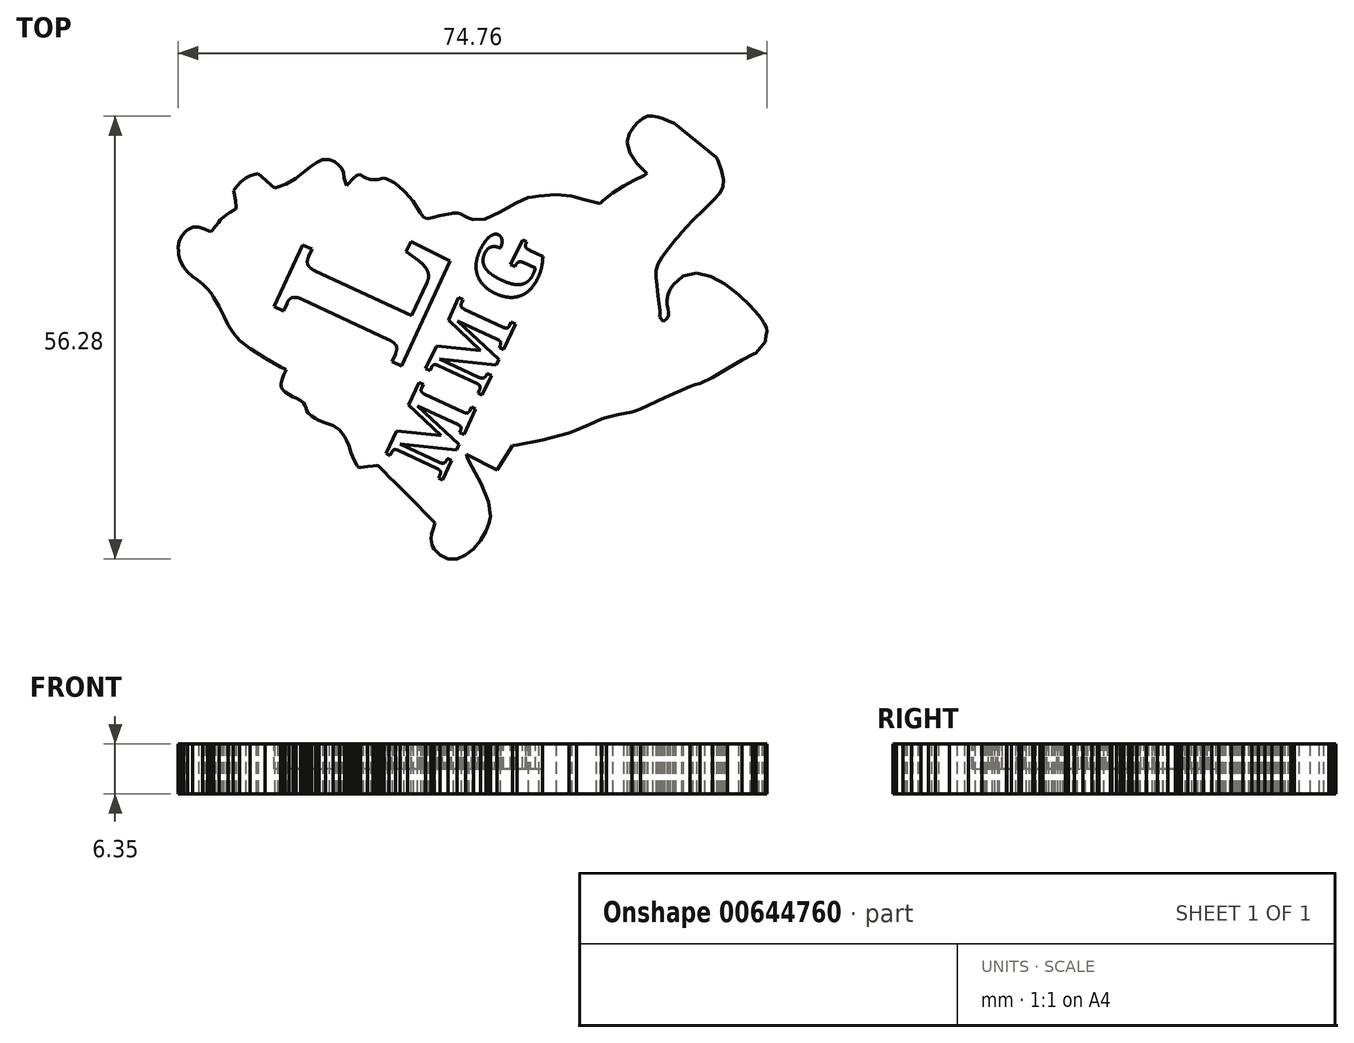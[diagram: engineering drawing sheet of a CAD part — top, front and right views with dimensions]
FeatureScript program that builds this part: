
annotation { "Feature Type Name" : "Feature", "Feature Type Description" : "" }
export const myFeature = defineFeature(function(context is Context, id is Id, definition is map)
    precondition{}
    {
        {
            var Q0;
            Q0=qCreatedBy(makeId("Top.planeOp"),FACE);
            var sketch = newSketch(context, id + "F0", { "sketchPlane" : qUnion([Q0])});
            skLineSegment(sketch, "E0", {"start": v(36, -1.99) * mm, "end": v(37.2, -0.53) * mm});
            skLineSegment(sketch, "E1", {"start": v(37.2, -0.53) * mm, "end": v(37.2, -0.33) * mm});
            skLineSegment(sketch, "E2", {"start": v(37.2, -0.33) * mm, "end": v(37.29, 0.26) * mm});
            skLineSegment(sketch, "E3", {"start": v(37.29, 0.26) * mm, "end": v(37.38, 0.75) * mm});
            skLineSegment(sketch, "E4", {"start": v(37.38, 0.75) * mm, "end": v(37.3, 1.24) * mm});
            skLineSegment(sketch, "E5", {"start": v(37.3, 1.24) * mm, "end": v(37, 1.85) * mm});
            skLineSegment(sketch, "E6", {"start": v(37, 1.85) * mm, "end": v(36.9, 2.04) * mm});
            skLineSegment(sketch, "E7", {"start": v(36.9, 2.04) * mm, "end": v(36.76, 2.25) * mm});
            skLineSegment(sketch, "E8", {"start": v(36.76, 2.25) * mm, "end": v(36.3, 2.84) * mm});
            skLineSegment(sketch, "E9", {"start": v(36.3, 2.84) * mm, "end": v(35.23, 4.06) * mm});
            skLineSegment(sketch, "E10", {"start": v(35.23, 4.06) * mm, "end": v(33.79, 5.46) * mm});
            skLineSegment(sketch, "E11", {"start": v(33.79, 5.46) * mm, "end": v(32.1, 6.77) * mm});
            skLineSegment(sketch, "E12", {"start": v(32.1, 6.77) * mm, "end": v(30.27, 7.76) * mm});
            skLineSegment(sketch, "E13", {"start": v(30.27, 7.76) * mm, "end": v(28.44, 8.18) * mm});
            skLineSegment(sketch, "E14", {"start": v(28.44, 8.18) * mm, "end": v(26.72, 7.78) * mm});
            skLineSegment(sketch, "E15", {"start": v(26.72, 7.78) * mm, "end": v(25.5, 6.74) * mm});
            skLineSegment(sketch, "E16", {"start": v(25.5, 6.74) * mm, "end": v(25.23, 6.3) * mm});
            skLineSegment(sketch, "E17", {"start": v(25.23, 6.3) * mm, "end": v(25.1, 6.12) * mm});
            skLineSegment(sketch, "E18", {"start": v(25.1, 6.12) * mm, "end": v(24.82, 5.48) * mm});
            skLineSegment(sketch, "E19", {"start": v(24.82, 5.48) * mm, "end": v(24.68, 4.78) * mm});
            skLineSegment(sketch, "E20", {"start": v(24.68, 4.78) * mm, "end": v(24.7, 4.17) * mm});
            skLineSegment(sketch, "E21", {"start": v(24.7, 4.17) * mm, "end": v(24.8, 3.65) * mm});
            skLineSegment(sketch, "E22", {"start": v(24.8, 3.65) * mm, "end": v(24.9, 3.2) * mm});
            skLineSegment(sketch, "E23", {"start": v(24.9, 3.2) * mm, "end": v(24.9, 2.8) * mm});
            skLineSegment(sketch, "E24", {"start": v(24.9, 2.8) * mm, "end": v(24.7, 2.42) * mm});
            skLineSegment(sketch, "E25", {"start": v(24.7, 2.42) * mm, "end": v(24.35, 2.14) * mm});
            skLineSegment(sketch, "E26", {"start": v(24.35, 2.14) * mm, "end": v(24.22, 2.07) * mm});
            skLineSegment(sketch, "E27", {"start": v(24.22, 2.07) * mm, "end": v(24.13, 2.18) * mm});
            skLineSegment(sketch, "E28", {"start": v(24.13, 2.18) * mm, "end": v(23.84, 2.5) * mm});
            skLineSegment(sketch, "E29", {"start": v(23.84, 2.5) * mm, "end": v(23.75, 2.6) * mm});
            skLineSegment(sketch, "E30", {"start": v(23.75, 2.6) * mm, "end": v(23.8, 2.8) * mm});
            skLineSegment(sketch, "E31", {"start": v(23.8, 2.8) * mm, "end": v(23.8, 3.28) * mm});
            skLineSegment(sketch, "E32", {"start": v(23.8, 3.28) * mm, "end": v(23.8, 3.44) * mm});
            skLineSegment(sketch, "E33", {"start": v(23.8, 3.44) * mm, "end": v(23.75, 3.9) * mm});
            skLineSegment(sketch, "E34", {"start": v(23.75, 3.9) * mm, "end": v(23.58, 5.26) * mm});
            skLineSegment(sketch, "E35", {"start": v(23.58, 5.26) * mm, "end": v(23.4, 6.62) * mm});
            skLineSegment(sketch, "E36", {"start": v(23.4, 6.62) * mm, "end": v(23.28, 7.67) * mm});
            skLineSegment(sketch, "E37", {"start": v(23.28, 7.67) * mm, "end": v(23.31, 8.52) * mm});
            skLineSegment(sketch, "E38", {"start": v(23.31, 8.52) * mm, "end": v(23.55, 9.33) * mm});
            skLineSegment(sketch, "E39", {"start": v(23.55, 9.33) * mm, "end": v(24.04, 10.22) * mm});
            skLineSegment(sketch, "E40", {"start": v(24.04, 10.22) * mm, "end": v(24.86, 11.32) * mm});
            skLineSegment(sketch, "E41", {"start": v(24.86, 11.32) * mm, "end": v(25.77, 12.41) * mm});
            skLineSegment(sketch, "E42", {"start": v(25.77, 12.41) * mm, "end": v(26.07, 12.77) * mm});
            skLineSegment(sketch, "E43", {"start": v(26.07, 12.77) * mm, "end": v(26.53, 13.3) * mm});
            skLineSegment(sketch, "E44", {"start": v(26.53, 13.3) * mm, "end": v(27.95, 14.84) * mm});
            skLineSegment(sketch, "E45", {"start": v(27.95, 14.84) * mm, "end": v(29.45, 16.34) * mm});
            skLineSegment(sketch, "E46", {"start": v(29.45, 16.34) * mm, "end": v(30.6, 17.44) * mm});
            skLineSegment(sketch, "E47", {"start": v(30.6, 17.44) * mm, "end": v(31.39, 18.31) * mm});
            skLineSegment(sketch, "E48", {"start": v(31.39, 18.31) * mm, "end": v(31.82, 19.12) * mm});
            skLineSegment(sketch, "E49", {"start": v(31.82, 19.12) * mm, "end": v(31.9, 20.03) * mm});
            skLineSegment(sketch, "E50", {"start": v(31.9, 20.03) * mm, "end": v(31.62, 21.22) * mm});
            skLineSegment(sketch, "E51", {"start": v(31.62, 21.22) * mm, "end": v(31.16, 22.44) * mm});
            skLineSegment(sketch, "E52", {"start": v(31.16, 22.44) * mm, "end": v(30.99, 22.84) * mm});
            skLineSegment(sketch, "E53", {"start": v(30.99, 22.84) * mm, "end": v(25.6, 27.24) * mm});
            skLineSegment(sketch, "E54", {"start": v(25.6, 27.24) * mm, "end": v(25.42, 27.3) * mm});
            skLineSegment(sketch, "E55", {"start": v(25.42, 27.3) * mm, "end": v(24.88, 27.5) * mm});
            skLineSegment(sketch, "E56", {"start": v(24.88, 27.5) * mm, "end": v(24.2, 27.79) * mm});
            skLineSegment(sketch, "E57", {"start": v(24.2, 27.79) * mm, "end": v(23.53, 28.02) * mm});
            skLineSegment(sketch, "E58", {"start": v(23.53, 28.02) * mm, "end": v(22.88, 28.14) * mm});
            skLineSegment(sketch, "E59", {"start": v(22.88, 28.14) * mm, "end": v(22.23, 28.1) * mm});
            skLineSegment(sketch, "E60", {"start": v(22.23, 28.1) * mm, "end": v(21.57, 27.81) * mm});
            skLineSegment(sketch, "E61", {"start": v(21.57, 27.81) * mm, "end": v(20.89, 27.24) * mm});
            skLineSegment(sketch, "E62", {"start": v(20.89, 27.24) * mm, "end": v(20.33, 26.55) * mm});
            skLineSegment(sketch, "E63", {"start": v(20.33, 26.55) * mm, "end": v(20.17, 26.3) * mm});
            skLineSegment(sketch, "E64", {"start": v(20.17, 26.3) * mm, "end": v(19.96, 25.98) * mm});
            skLineSegment(sketch, "E65", {"start": v(19.96, 25.98) * mm, "end": v(19.65, 24.8) * mm});
            skLineSegment(sketch, "E66", {"start": v(19.65, 24.8) * mm, "end": v(19.97, 23.43) * mm});
            skLineSegment(sketch, "E67", {"start": v(19.97, 23.43) * mm, "end": v(20.89, 22.11) * mm});
            skLineSegment(sketch, "E68", {"start": v(20.89, 22.11) * mm, "end": v(21.84, 21.12) * mm});
            skLineSegment(sketch, "E69", {"start": v(21.84, 21.12) * mm, "end": v(22.18, 20.8) * mm});
            skLineSegment(sketch, "E70", {"start": v(22.18, 20.8) * mm, "end": v(21.78, 20.59) * mm});
            skLineSegment(sketch, "E71", {"start": v(21.78, 20.59) * mm, "end": v(20.56, 19.98) * mm});
            skLineSegment(sketch, "E72", {"start": v(20.56, 19.98) * mm, "end": v(19.14, 19.26) * mm});
            skLineSegment(sketch, "E73", {"start": v(19.14, 19.26) * mm, "end": v(17.75, 18.35) * mm});
            skLineSegment(sketch, "E74", {"start": v(17.75, 18.35) * mm, "end": v(16.58, 17.37) * mm});
            skLineSegment(sketch, "E75", {"start": v(16.58, 17.37) * mm, "end": v(16.22, 17.02) * mm});
            skLineSegment(sketch, "E76", {"start": v(16.22, 17.02) * mm, "end": v(15.7, 17.11) * mm});
            skLineSegment(sketch, "E77", {"start": v(15.7, 17.11) * mm, "end": v(14.18, 17.51) * mm});
            skLineSegment(sketch, "E78", {"start": v(14.18, 17.51) * mm, "end": v(12.57, 17.95) * mm});
            skLineSegment(sketch, "E79", {"start": v(12.57, 17.95) * mm, "end": v(10.63, 18.13) * mm});
            skLineSegment(sketch, "E80", {"start": v(10.63, 18.13) * mm, "end": v(8.36, 17.97) * mm});
            skLineSegment(sketch, "E81", {"start": v(8.36, 17.97) * mm, "end": v(7.62, 17.86) * mm});
            skLineSegment(sketch, "E82", {"start": v(7.62, 17.86) * mm, "end": v(7.07, 17.77) * mm});
            skLineSegment(sketch, "E83", {"start": v(7.07, 17.77) * mm, "end": v(5.49, 17.1) * mm});
            skLineSegment(sketch, "E84", {"start": v(5.49, 17.1) * mm, "end": v(3.52, 15.94) * mm});
            skLineSegment(sketch, "E85", {"start": v(3.52, 15.94) * mm, "end": v(1.6, 15.06) * mm});
            skLineSegment(sketch, "E86", {"start": v(1.6, 15.06) * mm, "end": v(0.08, 14.95) * mm});
            skLineSegment(sketch, "E87", {"start": v(0.08, 14.95) * mm, "end": v(-0.35, 15.1) * mm});
            skLineSegment(sketch, "E88", {"start": v(-0.35, 15.1) * mm, "end": v(-0.53, 15.17) * mm});
            skLineSegment(sketch, "E89", {"start": v(-0.53, 15.17) * mm, "end": v(-1.03, 15.43) * mm});
            skLineSegment(sketch, "E90", {"start": v(-1.03, 15.43) * mm, "end": v(-1.44, 15.68) * mm});
            skLineSegment(sketch, "E91", {"start": v(-1.44, 15.68) * mm, "end": v(-1.9, 15.81) * mm});
            skLineSegment(sketch, "E92", {"start": v(-1.9, 15.81) * mm, "end": v(-2.48, 15.78) * mm});
            skLineSegment(sketch, "E93", {"start": v(-2.48, 15.78) * mm, "end": v(-2.67, 15.75) * mm});
            skLineSegment(sketch, "E94", {"start": v(-2.67, 15.75) * mm, "end": v(-3.03, 15.68) * mm});
            skLineSegment(sketch, "E95", {"start": v(-3.03, 15.68) * mm, "end": v(-4.11, 15.47) * mm});
            skLineSegment(sketch, "E96", {"start": v(-4.11, 15.47) * mm, "end": v(-5.07, 15.25) * mm});
            skLineSegment(sketch, "E97", {"start": v(-5.07, 15.25) * mm, "end": v(-5.67, 15.14) * mm});
            skLineSegment(sketch, "E98", {"start": v(-5.67, 15.14) * mm, "end": v(-6.05, 15.17) * mm});
            skLineSegment(sketch, "E99", {"start": v(-6.05, 15.17) * mm, "end": v(-6.32, 15.38) * mm});
            skLineSegment(sketch, "E100", {"start": v(-6.32, 15.38) * mm, "end": v(-6.61, 15.82) * mm});
            skLineSegment(sketch, "E101", {"start": v(-6.61, 15.82) * mm, "end": v(-7.05, 16.53) * mm});
            skLineSegment(sketch, "E102", {"start": v(-7.05, 16.53) * mm, "end": v(-7.56, 17.3) * mm});
            skLineSegment(sketch, "E103", {"start": v(-7.56, 17.3) * mm, "end": v(-7.75, 17.54) * mm});
            skLineSegment(sketch, "E104", {"start": v(-7.75, 17.54) * mm, "end": v(-7.87, 17.7) * mm});
            skLineSegment(sketch, "E105", {"start": v(-7.87, 17.7) * mm, "end": v(-8.74, 18.65) * mm});
            skLineSegment(sketch, "E106", {"start": v(-8.74, 18.65) * mm, "end": v(-9.8, 19.52) * mm});
            skLineSegment(sketch, "E107", {"start": v(-9.8, 19.52) * mm, "end": v(-10, 19.65) * mm});
            skLineSegment(sketch, "E108", {"start": v(-10, 19.65) * mm, "end": v(-10.2, 19.78) * mm});
            skLineSegment(sketch, "E109", {"start": v(-10.2, 19.78) * mm, "end": v(-10.84, 20.13) * mm});
            skLineSegment(sketch, "E110", {"start": v(-10.84, 20.13) * mm, "end": v(-11.25, 20.24) * mm});
            skLineSegment(sketch, "E111", {"start": v(-11.25, 20.24) * mm, "end": v(-11.57, 20.16) * mm});
            skLineSegment(sketch, "E112", {"start": v(-11.57, 20.16) * mm, "end": v(-11.98, 20.06) * mm});
            skLineSegment(sketch, "E113", {"start": v(-11.98, 20.06) * mm, "end": v(-12.12, 20.05) * mm});
            skLineSegment(sketch, "E114", {"start": v(-12.12, 20.05) * mm, "end": v(-12.33, 20.04) * mm});
            skLineSegment(sketch, "E115", {"start": v(-12.33, 20.04) * mm, "end": v(-12.96, 20.07) * mm});
            skLineSegment(sketch, "E116", {"start": v(-12.96, 20.07) * mm, "end": v(-13.51, 20.24) * mm});
            skLineSegment(sketch, "E117", {"start": v(-13.51, 20.24) * mm, "end": v(-13.88, 20.47) * mm});
            skLineSegment(sketch, "E118", {"start": v(-13.88, 20.47) * mm, "end": v(-14.15, 20.66) * mm});
            skLineSegment(sketch, "E119", {"start": v(-14.15, 20.66) * mm, "end": v(-14.41, 20.72) * mm});
            skLineSegment(sketch, "E120", {"start": v(-14.41, 20.72) * mm, "end": v(-14.74, 20.58) * mm});
            skLineSegment(sketch, "E121", {"start": v(-14.74, 20.58) * mm, "end": v(-15.24, 20.13) * mm});
            skLineSegment(sketch, "E122", {"start": v(-15.24, 20.13) * mm, "end": v(-15.8, 19.5) * mm});
            skLineSegment(sketch, "E123", {"start": v(-15.8, 19.5) * mm, "end": v(-15.99, 19.29) * mm});
            skLineSegment(sketch, "E124", {"start": v(-15.99, 19.29) * mm, "end": v(-16.1, 19.5) * mm});
            skLineSegment(sketch, "E125", {"start": v(-16.1, 19.5) * mm, "end": v(-16.3, 20.22) * mm});
            skLineSegment(sketch, "E126", {"start": v(-16.3, 20.22) * mm, "end": v(-16.4, 20.93) * mm});
            skLineSegment(sketch, "E127", {"start": v(-16.4, 20.93) * mm, "end": v(-16.64, 21.53) * mm});
            skLineSegment(sketch, "E128", {"start": v(-16.64, 21.53) * mm, "end": v(-17.15, 22.05) * mm});
            skLineSegment(sketch, "E129", {"start": v(-17.15, 22.05) * mm, "end": v(-17.34, 22.18) * mm});
            skLineSegment(sketch, "E130", {"start": v(-17.34, 22.18) * mm, "end": v(-17.55, 22.32) * mm});
            skLineSegment(sketch, "E131", {"start": v(-17.55, 22.32) * mm, "end": v(-18.25, 22.6) * mm});
            skLineSegment(sketch, "E132", {"start": v(-18.25, 22.6) * mm, "end": v(-19.07, 22.57) * mm});
            skLineSegment(sketch, "E133", {"start": v(-19.07, 22.57) * mm, "end": v(-19.85, 22.22) * mm});
            skLineSegment(sketch, "E134", {"start": v(-19.85, 22.22) * mm, "end": v(-20.64, 21.63) * mm});
            skLineSegment(sketch, "E135", {"start": v(-20.64, 21.63) * mm, "end": v(-21.5, 20.92) * mm});
            skLineSegment(sketch, "E136", {"start": v(-21.5, 20.92) * mm, "end": v(-22.5, 20.17) * mm});
            skLineSegment(sketch, "E137", {"start": v(-22.5, 20.17) * mm, "end": v(-23.7, 19.5) * mm});
            skLineSegment(sketch, "E138", {"start": v(-23.7, 19.5) * mm, "end": v(-24.78, 19.1) * mm});
            skLineSegment(sketch, "E139", {"start": v(-24.78, 19.1) * mm, "end": v(-25.15, 19) * mm});
            skLineSegment(sketch, "E140", {"start": v(-25.15, 19) * mm, "end": v(-27.25, 20.81) * mm});
            skLineSegment(sketch, "E141", {"start": v(-27.25, 20.81) * mm, "end": v(-27.48, 20.75) * mm});
            skLineSegment(sketch, "E142", {"start": v(-27.48, 20.75) * mm, "end": v(-28.18, 20.56) * mm});
            skLineSegment(sketch, "E143", {"start": v(-28.18, 20.56) * mm, "end": v(-28.85, 20.24) * mm});
            skLineSegment(sketch, "E144", {"start": v(-28.85, 20.24) * mm, "end": v(-29.5, 19.67) * mm});
            skLineSegment(sketch, "E145", {"start": v(-29.5, 19.67) * mm, "end": v(-30.17, 18.9) * mm});
            skLineSegment(sketch, "E146", {"start": v(-30.17, 18.9) * mm, "end": v(-30.38, 18.64) * mm});
            skLineSegment(sketch, "E147", {"start": v(-30.38, 18.64) * mm, "end": v(-30.32, 18.41) * mm});
            skLineSegment(sketch, "E148", {"start": v(-30.32, 18.41) * mm, "end": v(-30.1, 17.38) * mm});
            skLineSegment(sketch, "E149", {"start": v(-30.1, 17.38) * mm, "end": v(-30.06, 16.48) * mm});
            skLineSegment(sketch, "E150", {"start": v(-30.06, 16.48) * mm, "end": v(-30.09, 16.33) * mm});
            skLineSegment(sketch, "E151", {"start": v(-30.09, 16.33) * mm, "end": v(-30.27, 16.21) * mm});
            skLineSegment(sketch, "E152", {"start": v(-30.27, 16.21) * mm, "end": v(-30.83, 15.86) * mm});
            skLineSegment(sketch, "E153", {"start": v(-30.83, 15.86) * mm, "end": v(-31.33, 15.55) * mm});
            skLineSegment(sketch, "E154", {"start": v(-31.33, 15.55) * mm, "end": v(-31.64, 15.32) * mm});
            skLineSegment(sketch, "E155", {"start": v(-31.64, 15.32) * mm, "end": v(-31.85, 15.13) * mm});
            skLineSegment(sketch, "E156", {"start": v(-31.85, 15.13) * mm, "end": v(-32.04, 14.9) * mm});
            skLineSegment(sketch, "E157", {"start": v(-32.04, 14.9) * mm, "end": v(-32.28, 14.59) * mm});
            skLineSegment(sketch, "E158", {"start": v(-32.28, 14.59) * mm, "end": v(-32.66, 14.12) * mm});
            skLineSegment(sketch, "E159", {"start": v(-32.66, 14.12) * mm, "end": v(-33.09, 13.61) * mm});
            skLineSegment(sketch, "E160", {"start": v(-33.09, 13.61) * mm, "end": v(-33.23, 13.44) * mm});
            skLineSegment(sketch, "E161", {"start": v(-33.23, 13.44) * mm, "end": v(-33.45, 13.52) * mm});
            skLineSegment(sketch, "E162", {"start": v(-33.45, 13.52) * mm, "end": v(-34.07, 13.78) * mm});
            skLineSegment(sketch, "E163", {"start": v(-34.07, 13.78) * mm, "end": v(-34.79, 14.03) * mm});
            skLineSegment(sketch, "E164", {"start": v(-34.79, 14.03) * mm, "end": v(-35.5, 14.03) * mm});
            skLineSegment(sketch, "E165", {"start": v(-35.5, 14.03) * mm, "end": v(-36.13, 13.73) * mm});
            skLineSegment(sketch, "E166", {"start": v(-36.13, 13.73) * mm, "end": v(-36.3, 13.58) * mm});
            skLineSegment(sketch, "E167", {"start": v(-36.3, 13.58) * mm, "end": v(-36.49, 13.44) * mm});
            skLineSegment(sketch, "E168", {"start": v(-36.49, 13.44) * mm, "end": v(-36.94, 12.91) * mm});
            skLineSegment(sketch, "E169", {"start": v(-36.94, 12.91) * mm, "end": v(-37.27, 12.19) * mm});
            skLineSegment(sketch, "E170", {"start": v(-37.27, 12.19) * mm, "end": v(-37.38, 11.46) * mm});
            skLineSegment(sketch, "E171", {"start": v(-37.38, 11.46) * mm, "end": v(-37.37, 10.94) * mm});
            skLineSegment(sketch, "E172", {"start": v(-37.37, 10.94) * mm, "end": v(-37.35, 10.77) * mm});
            skLineSegment(sketch, "E173", {"start": v(-37.35, 10.77) * mm, "end": v(-37.32, 10.52) * mm});
            skLineSegment(sketch, "E174", {"start": v(-37.32, 10.52) * mm, "end": v(-37.13, 9.76) * mm});
            skLineSegment(sketch, "E175", {"start": v(-37.13, 9.76) * mm, "end": v(-36.73, 8.96) * mm});
            skLineSegment(sketch, "E176", {"start": v(-36.73, 8.96) * mm, "end": v(-36.21, 8.31) * mm});
            skLineSegment(sketch, "E177", {"start": v(-36.21, 8.31) * mm, "end": v(-35.6, 7.77) * mm});
            skLineSegment(sketch, "E178", {"start": v(-35.6, 7.77) * mm, "end": v(-34.94, 7.27) * mm});
            skLineSegment(sketch, "E179", {"start": v(-34.94, 7.27) * mm, "end": v(-34.28, 6.76) * mm});
            skLineSegment(sketch, "E180", {"start": v(-34.28, 6.76) * mm, "end": v(-33.65, 6.18) * mm});
            skLineSegment(sketch, "E181", {"start": v(-33.65, 6.18) * mm, "end": v(-33.23, 5.67) * mm});
            skLineSegment(sketch, "E182", {"start": v(-33.23, 5.67) * mm, "end": v(-33.1, 5.48) * mm});
            skLineSegment(sketch, "E183", {"start": v(-33.1, 5.48) * mm, "end": v(-32.87, 5.1) * mm});
            skLineSegment(sketch, "E184", {"start": v(-32.87, 5.1) * mm, "end": v(-32.22, 3.93) * mm});
            skLineSegment(sketch, "E185", {"start": v(-32.22, 3.93) * mm, "end": v(-31.6, 2.66) * mm});
            skLineSegment(sketch, "E186", {"start": v(-31.6, 2.66) * mm, "end": v(-31.06, 1.58) * mm});
            skLineSegment(sketch, "E187", {"start": v(-31.06, 1.58) * mm, "end": v(-30.44, 0.6) * mm});
            skLineSegment(sketch, "E188", {"start": v(-30.44, 0.6) * mm, "end": v(-29.57, -0.36) * mm});
            skLineSegment(sketch, "E189", {"start": v(-29.57, -0.36) * mm, "end": v(-28.27, -1.4) * mm});
            skLineSegment(sketch, "E190", {"start": v(-28.27, -1.4) * mm, "end": v(-26.37, -2.62) * mm});
            skLineSegment(sketch, "E191", {"start": v(-26.37, -2.62) * mm, "end": v(-24.37, -3.74) * mm});
            skLineSegment(sketch, "E192", {"start": v(-24.37, -3.74) * mm, "end": v(-23.7, -4.1) * mm});
            skLineSegment(sketch, "E193", {"start": v(-23.7, -4.1) * mm, "end": v(-23.77, -4.27) * mm});
            skLineSegment(sketch, "E194", {"start": v(-23.77, -4.27) * mm, "end": v(-23.99, -4.78) * mm});
            skLineSegment(sketch, "E195", {"start": v(-23.99, -4.78) * mm, "end": v(-24.2, -5.35) * mm});
            skLineSegment(sketch, "E196", {"start": v(-24.2, -5.35) * mm, "end": v(-24.32, -5.82) * mm});
            skLineSegment(sketch, "E197", {"start": v(-24.32, -5.82) * mm, "end": v(-24.32, -6.23) * mm});
            skLineSegment(sketch, "E198", {"start": v(-24.32, -6.23) * mm, "end": v(-24.16, -6.58) * mm});
            skLineSegment(sketch, "E199", {"start": v(-24.16, -6.58) * mm, "end": v(-23.84, -6.92) * mm});
            skLineSegment(sketch, "E200", {"start": v(-23.84, -6.92) * mm, "end": v(-23.33, -7.26) * mm});
            skLineSegment(sketch, "E201", {"start": v(-23.33, -7.26) * mm, "end": v(-22.78, -7.54) * mm});
            skLineSegment(sketch, "E202", {"start": v(-22.78, -7.54) * mm, "end": v(-22.6, -7.62) * mm});
            skLineSegment(sketch, "E203", {"start": v(-22.6, -7.62) * mm, "end": v(-22.41, -7.7) * mm});
            skLineSegment(sketch, "E204", {"start": v(-22.41, -7.7) * mm, "end": v(-21.87, -8) * mm});
            skLineSegment(sketch, "E205", {"start": v(-21.87, -8) * mm, "end": v(-21.46, -8.35) * mm});
            skLineSegment(sketch, "E206", {"start": v(-21.46, -8.35) * mm, "end": v(-21.25, -8.66) * mm});
            skLineSegment(sketch, "E207", {"start": v(-21.25, -8.66) * mm, "end": v(-21.16, -8.97) * mm});
            skLineSegment(sketch, "E208", {"start": v(-21.16, -8.97) * mm, "end": v(-21.06, -9.27) * mm});
            skLineSegment(sketch, "E209", {"start": v(-21.06, -9.27) * mm, "end": v(-20.87, -9.6) * mm});
            skLineSegment(sketch, "E210", {"start": v(-20.87, -9.6) * mm, "end": v(-20.48, -9.98) * mm});
            skLineSegment(sketch, "E211", {"start": v(-20.48, -9.98) * mm, "end": v(-19.96, -10.3) * mm});
            skLineSegment(sketch, "E212", {"start": v(-19.96, -10.3) * mm, "end": v(-19.78, -10.4) * mm});
            skLineSegment(sketch, "E213", {"start": v(-19.78, -10.4) * mm, "end": v(-19.52, -10.54) * mm});
            skLineSegment(sketch, "E214", {"start": v(-19.52, -10.54) * mm, "end": v(-18.68, -10.86) * mm});
            skLineSegment(sketch, "E215", {"start": v(-18.68, -10.86) * mm, "end": v(-17.73, -11.21) * mm});
            skLineSegment(sketch, "E216", {"start": v(-17.73, -11.21) * mm, "end": v(-16.88, -11.77) * mm});
            skLineSegment(sketch, "E217", {"start": v(-16.88, -11.77) * mm, "end": v(-16.26, -12.56) * mm});
            skLineSegment(sketch, "E218", {"start": v(-16.26, -12.56) * mm, "end": v(-16.1, -12.86) * mm});
            skLineSegment(sketch, "E219", {"start": v(-16.1, -12.86) * mm, "end": v(-15.99, -13.08) * mm});
            skLineSegment(sketch, "E220", {"start": v(-15.99, -13.08) * mm, "end": v(-15.7, -13.8) * mm});
            skLineSegment(sketch, "E221", {"start": v(-15.7, -13.8) * mm, "end": v(-15.42, -14.67) * mm});
            skLineSegment(sketch, "E222", {"start": v(-15.42, -14.67) * mm, "end": v(-15.07, -15.54) * mm});
            skLineSegment(sketch, "E223", {"start": v(-15.07, -15.54) * mm, "end": v(-14.65, -16.28) * mm});
            skLineSegment(sketch, "E224", {"start": v(-14.65, -16.28) * mm, "end": v(-14.49, -16.51) * mm});
            skLineSegment(sketch, "E225", {"start": v(-14.49, -16.51) * mm, "end": v(-14.2, -16.5) * mm});
            skLineSegment(sketch, "E226", {"start": v(-14.2, -16.5) * mm, "end": v(-13.36, -16.42) * mm});
            skLineSegment(sketch, "E227", {"start": v(-13.36, -16.42) * mm, "end": v(-12.65, -16.32) * mm});
            skLineSegment(sketch, "E228", {"start": v(-12.65, -16.32) * mm, "end": v(-12.22, -16.28) * mm});
            skLineSegment(sketch, "E229", {"start": v(-12.22, -16.28) * mm, "end": v(-11.94, -16.34) * mm});
            skLineSegment(sketch, "E230", {"start": v(-11.94, -16.34) * mm, "end": v(-11.66, -16.56) * mm});
            skLineSegment(sketch, "E231", {"start": v(-11.66, -16.56) * mm, "end": v(-11.26, -17) * mm});
            skLineSegment(sketch, "E232", {"start": v(-11.26, -17) * mm, "end": v(-10.6, -17.72) * mm});
            skLineSegment(sketch, "E233", {"start": v(-10.6, -17.72) * mm, "end": v(-9.8, -18.51) * mm});
            skLineSegment(sketch, "E234", {"start": v(-9.8, -18.51) * mm, "end": v(-9.52, -18.77) * mm});
            skLineSegment(sketch, "E235", {"start": v(-9.52, -18.77) * mm, "end": v(-9.2, -19.07) * mm});
            skLineSegment(sketch, "E236", {"start": v(-9.2, -19.07) * mm, "end": v(-8.25, -20) * mm});
            skLineSegment(sketch, "E237", {"start": v(-8.25, -20) * mm, "end": v(-7.1, -21.18) * mm});
            skLineSegment(sketch, "E238", {"start": v(-7.1, -21.18) * mm, "end": v(-5.98, -22.34) * mm});
            skLineSegment(sketch, "E239", {"start": v(-5.98, -22.34) * mm, "end": v(-5.07, -23.25) * mm});
            skLineSegment(sketch, "E240", {"start": v(-5.07, -23.25) * mm, "end": v(-4.76, -23.55) * mm});
            skLineSegment(sketch, "E241", {"start": v(-4.76, -23.55) * mm, "end": v(-4.8, -23.76) * mm});
            skLineSegment(sketch, "E242", {"start": v(-4.8, -23.76) * mm, "end": v(-5, -24.36) * mm});
            skLineSegment(sketch, "E243", {"start": v(-5, -24.36) * mm, "end": v(-5.2, -24.98) * mm});
            skLineSegment(sketch, "E244", {"start": v(-5.2, -24.98) * mm, "end": v(-5.26, -25.63) * mm});
            skLineSegment(sketch, "E245", {"start": v(-5.26, -25.63) * mm, "end": v(-5.16, -26.33) * mm});
            skLineSegment(sketch, "E246", {"start": v(-5.16, -26.33) * mm, "end": v(-5.1, -26.55) * mm});
            skLineSegment(sketch, "E247", {"start": v(-5.1, -26.55) * mm, "end": v(-4.92, -26.86) * mm});
            skLineSegment(sketch, "E248", {"start": v(-4.92, -26.86) * mm, "end": v(-4.15, -27.65) * mm});
            skLineSegment(sketch, "E249", {"start": v(-4.15, -27.65) * mm, "end": v(-3.1, -28.14) * mm});
            skLineSegment(sketch, "E250", {"start": v(-3.1, -28.14) * mm, "end": v(-1.99, -28.11) * mm});
            skLineSegment(sketch, "E251", {"start": v(-1.99, -28.11) * mm, "end": v(-0.9, -27.65) * mm});
            skLineSegment(sketch, "E252", {"start": v(-0.9, -27.65) * mm, "end": v(0.13, -26.85) * mm});
            skLineSegment(sketch, "E253", {"start": v(0.13, -26.85) * mm, "end": v(1.02, -25.8) * mm});
            skLineSegment(sketch, "E254", {"start": v(1.02, -25.8) * mm, "end": v(1.71, -24.57) * mm});
            skLineSegment(sketch, "E255", {"start": v(1.71, -24.57) * mm, "end": v(2.08, -23.6) * mm});
            skLineSegment(sketch, "E256", {"start": v(2.08, -23.6) * mm, "end": v(2.16, -23.26) * mm});
            skLineSegment(sketch, "E257", {"start": v(2.16, -23.26) * mm, "end": v(2.28, -22.72) * mm});
            skLineSegment(sketch, "E258", {"start": v(2.28, -22.72) * mm, "end": v(2.03, -20.93) * mm});
            skLineSegment(sketch, "E259", {"start": v(2.03, -20.93) * mm, "end": v(1.07, -18.56) * mm});
            skLineSegment(sketch, "E260", {"start": v(1.07, -18.56) * mm, "end": v(-0.07, -16.43) * mm});
            skLineSegment(sketch, "E261", {"start": v(-0.07, -16.43) * mm, "end": v(-0.68, -15.26) * mm});
            skLineSegment(sketch, "E262", {"start": v(-0.68, -15.26) * mm, "end": v(-0.76, -14.85) * mm});
            skLineSegment(sketch, "E263", {"start": v(-0.76, -14.85) * mm, "end": v(3.1, -16.84) * mm});
            skLineSegment(sketch, "E264", {"start": v(3.1, -16.84) * mm, "end": v(5.05, -13.71) * mm});
            skLineSegment(sketch, "E265", {"start": v(5.05, -13.71) * mm, "end": v(5.62, -13.66) * mm});
            skLineSegment(sketch, "E266", {"start": v(5.62, -13.66) * mm, "end": v(8.9, -13.05) * mm});
            skLineSegment(sketch, "E267", {"start": v(8.9, -13.05) * mm, "end": v(12.27, -12.12) * mm});
            skLineSegment(sketch, "E268", {"start": v(12.27, -12.12) * mm, "end": v(12.88, -11.9) * mm});
            skLineSegment(sketch, "E269", {"start": v(12.88, -11.9) * mm, "end": v(13.23, -11.79) * mm});
            skLineSegment(sketch, "E270", {"start": v(13.23, -11.79) * mm, "end": v(14.83, -11.08) * mm});
            skLineSegment(sketch, "E271", {"start": v(14.83, -11.08) * mm, "end": v(16.4, -10.37) * mm});
            skLineSegment(sketch, "E272", {"start": v(16.4, -10.37) * mm, "end": v(16.73, -10.24) * mm});
            skLineSegment(sketch, "E273", {"start": v(16.73, -10.24) * mm, "end": v(17.01, -10.14) * mm});
            skLineSegment(sketch, "E274", {"start": v(17.01, -10.14) * mm, "end": v(18.54, -9.81) * mm});
            skLineSegment(sketch, "E275", {"start": v(18.54, -9.81) * mm, "end": v(20.26, -9.44) * mm});
            skLineSegment(sketch, "E276", {"start": v(20.26, -9.44) * mm, "end": v(20.63, -9.31) * mm});
            skLineSegment(sketch, "E277", {"start": v(20.63, -9.31) * mm, "end": v(21.3, -9.08) * mm});
            skLineSegment(sketch, "E278", {"start": v(21.3, -9.08) * mm, "end": v(24.47, -7.65) * mm});
            skLineSegment(sketch, "E279", {"start": v(24.47, -7.65) * mm, "end": v(27.64, -6.23) * mm});
            skLineSegment(sketch, "E280", {"start": v(27.64, -6.23) * mm, "end": v(28.3, -6) * mm});
            skLineSegment(sketch, "E281", {"start": v(28.3, -6) * mm, "end": v(28.86, -5.82) * mm});
            skLineSegment(sketch, "E282", {"start": v(28.86, -5.82) * mm, "end": v(30.46, -5.08) * mm});
            skLineSegment(sketch, "E283", {"start": v(30.46, -5.08) * mm, "end": v(32.4, -3.97) * mm});
            skLineSegment(sketch, "E284", {"start": v(32.4, -3.97) * mm, "end": v(34.2, -2.87) * mm});
            skLineSegment(sketch, "E285", {"start": v(34.2, -2.87) * mm, "end": v(35.54, -2.17) * mm});
            skLineSegment(sketch, "E286", {"start": v(35.54, -2.17) * mm, "end": v(36, -1.99) * mm});
            skSolve(sketch);
        }
        {
            var Q0;
            Q0=makeQuery(id+"F0.imprint","IMPRINT",FACE,{"disambiguationData":[TD([[makeQuery(id+"F0.imprint","IMPRINT",EDGE,{"derivedFrom":sQuery(id+"F0.wireOp",EDGE,"E0")}),1.0]])]});
            extrude(context, id + "F1", {"entities" : qUnion([Q0]), "depth" : 6.35 * mm, "offsetDistance" : 25.4 * mm});
        }
        {
            var Q0;
            Q0=makeQuery(id+"F1.opExtrude","CAP_FACE",FACE,{"disambiguationData":[OSD([sQuery(id+"F0.wireOp",EDGE,"E0"),sQuery(id+"F0.wireOp",EDGE,"E1"),sQuery(id+"F0.wireOp",EDGE,"E2"),sQuery(id+"F0.wireOp",EDGE,"E3"),sQuery(id+"F0.wireOp",EDGE,"E4"),sQuery(id+"F0.wireOp",EDGE,"E5"),sQuery(id+"F0.wireOp",EDGE,"E6"),sQuery(id+"F0.wireOp",EDGE,"E7"),sQuery(id+"F0.wireOp",EDGE,"E8"),sQuery(id+"F0.wireOp",EDGE,"E9"),sQuery(id+"F0.wireOp",EDGE,"E10"),sQuery(id+"F0.wireOp",EDGE,"E11"),sQuery(id+"F0.wireOp",EDGE,"E12"),sQuery(id+"F0.wireOp",EDGE,"E13"),sQuery(id+"F0.wireOp",EDGE,"E14"),sQuery(id+"F0.wireOp",EDGE,"E15"),sQuery(id+"F0.wireOp",EDGE,"E16"),sQuery(id+"F0.wireOp",EDGE,"E17"),sQuery(id+"F0.wireOp",EDGE,"E18"),sQuery(id+"F0.wireOp",EDGE,"E19"),sQuery(id+"F0.wireOp",EDGE,"E20"),sQuery(id+"F0.wireOp",EDGE,"E21"),sQuery(id+"F0.wireOp",EDGE,"E22"),sQuery(id+"F0.wireOp",EDGE,"E23"),sQuery(id+"F0.wireOp",EDGE,"E24"),sQuery(id+"F0.wireOp",EDGE,"E25"),sQuery(id+"F0.wireOp",EDGE,"E26"),sQuery(id+"F0.wireOp",EDGE,"E27"),sQuery(id+"F0.wireOp",EDGE,"E28"),sQuery(id+"F0.wireOp",EDGE,"E29"),sQuery(id+"F0.wireOp",EDGE,"E30"),sQuery(id+"F0.wireOp",EDGE,"E31"),sQuery(id+"F0.wireOp",EDGE,"E32"),sQuery(id+"F0.wireOp",EDGE,"E33"),sQuery(id+"F0.wireOp",EDGE,"E34"),sQuery(id+"F0.wireOp",EDGE,"E35"),sQuery(id+"F0.wireOp",EDGE,"E36"),sQuery(id+"F0.wireOp",EDGE,"E37"),sQuery(id+"F0.wireOp",EDGE,"E38"),sQuery(id+"F0.wireOp",EDGE,"E39"),sQuery(id+"F0.wireOp",EDGE,"E40"),sQuery(id+"F0.wireOp",EDGE,"E41"),sQuery(id+"F0.wireOp",EDGE,"E42"),sQuery(id+"F0.wireOp",EDGE,"E43"),sQuery(id+"F0.wireOp",EDGE,"E44"),sQuery(id+"F0.wireOp",EDGE,"E45"),sQuery(id+"F0.wireOp",EDGE,"E46"),sQuery(id+"F0.wireOp",EDGE,"E47"),sQuery(id+"F0.wireOp",EDGE,"E48"),sQuery(id+"F0.wireOp",EDGE,"E49"),sQuery(id+"F0.wireOp",EDGE,"E50"),sQuery(id+"F0.wireOp",EDGE,"E51"),sQuery(id+"F0.wireOp",EDGE,"E52"),sQuery(id+"F0.wireOp",EDGE,"E53"),sQuery(id+"F0.wireOp",EDGE,"E54"),sQuery(id+"F0.wireOp",EDGE,"E55"),sQuery(id+"F0.wireOp",EDGE,"E56"),sQuery(id+"F0.wireOp",EDGE,"E57"),sQuery(id+"F0.wireOp",EDGE,"E58"),sQuery(id+"F0.wireOp",EDGE,"E59"),sQuery(id+"F0.wireOp",EDGE,"E60"),sQuery(id+"F0.wireOp",EDGE,"E61"),sQuery(id+"F0.wireOp",EDGE,"E62"),sQuery(id+"F0.wireOp",EDGE,"E63"),sQuery(id+"F0.wireOp",EDGE,"E64"),sQuery(id+"F0.wireOp",EDGE,"E65"),sQuery(id+"F0.wireOp",EDGE,"E66"),sQuery(id+"F0.wireOp",EDGE,"E67"),sQuery(id+"F0.wireOp",EDGE,"E68"),sQuery(id+"F0.wireOp",EDGE,"E69"),sQuery(id+"F0.wireOp",EDGE,"E70"),sQuery(id+"F0.wireOp",EDGE,"E71"),sQuery(id+"F0.wireOp",EDGE,"E72"),sQuery(id+"F0.wireOp",EDGE,"E73"),sQuery(id+"F0.wireOp",EDGE,"E74"),sQuery(id+"F0.wireOp",EDGE,"E75"),sQuery(id+"F0.wireOp",EDGE,"E76"),sQuery(id+"F0.wireOp",EDGE,"E77"),sQuery(id+"F0.wireOp",EDGE,"E78"),sQuery(id+"F0.wireOp",EDGE,"E79"),sQuery(id+"F0.wireOp",EDGE,"E80"),sQuery(id+"F0.wireOp",EDGE,"E81"),sQuery(id+"F0.wireOp",EDGE,"E82"),sQuery(id+"F0.wireOp",EDGE,"E83"),sQuery(id+"F0.wireOp",EDGE,"E84"),sQuery(id+"F0.wireOp",EDGE,"E85"),sQuery(id+"F0.wireOp",EDGE,"E86"),sQuery(id+"F0.wireOp",EDGE,"E87"),sQuery(id+"F0.wireOp",EDGE,"E88"),sQuery(id+"F0.wireOp",EDGE,"E89"),sQuery(id+"F0.wireOp",EDGE,"E90"),sQuery(id+"F0.wireOp",EDGE,"E91"),sQuery(id+"F0.wireOp",EDGE,"E92"),sQuery(id+"F0.wireOp",EDGE,"E93"),sQuery(id+"F0.wireOp",EDGE,"E94"),sQuery(id+"F0.wireOp",EDGE,"E95"),sQuery(id+"F0.wireOp",EDGE,"E96"),sQuery(id+"F0.wireOp",EDGE,"E97"),sQuery(id+"F0.wireOp",EDGE,"E98"),sQuery(id+"F0.wireOp",EDGE,"E99"),sQuery(id+"F0.wireOp",EDGE,"E100"),sQuery(id+"F0.wireOp",EDGE,"E101"),sQuery(id+"F0.wireOp",EDGE,"E102"),sQuery(id+"F0.wireOp",EDGE,"E103"),sQuery(id+"F0.wireOp",EDGE,"E104"),sQuery(id+"F0.wireOp",EDGE,"E105"),sQuery(id+"F0.wireOp",EDGE,"E106"),sQuery(id+"F0.wireOp",EDGE,"E107"),sQuery(id+"F0.wireOp",EDGE,"E108"),sQuery(id+"F0.wireOp",EDGE,"E109"),sQuery(id+"F0.wireOp",EDGE,"E110"),sQuery(id+"F0.wireOp",EDGE,"E111"),sQuery(id+"F0.wireOp",EDGE,"E112"),sQuery(id+"F0.wireOp",EDGE,"E113"),sQuery(id+"F0.wireOp",EDGE,"E114"),sQuery(id+"F0.wireOp",EDGE,"E115"),sQuery(id+"F0.wireOp",EDGE,"E116"),sQuery(id+"F0.wireOp",EDGE,"E117"),sQuery(id+"F0.wireOp",EDGE,"E118"),sQuery(id+"F0.wireOp",EDGE,"E119"),sQuery(id+"F0.wireOp",EDGE,"E120"),sQuery(id+"F0.wireOp",EDGE,"E121"),sQuery(id+"F0.wireOp",EDGE,"E122"),sQuery(id+"F0.wireOp",EDGE,"E123"),sQuery(id+"F0.wireOp",EDGE,"E124"),sQuery(id+"F0.wireOp",EDGE,"E125"),sQuery(id+"F0.wireOp",EDGE,"E126"),sQuery(id+"F0.wireOp",EDGE,"E127"),sQuery(id+"F0.wireOp",EDGE,"E128"),sQuery(id+"F0.wireOp",EDGE,"E129"),sQuery(id+"F0.wireOp",EDGE,"E130"),sQuery(id+"F0.wireOp",EDGE,"E131"),sQuery(id+"F0.wireOp",EDGE,"E132"),sQuery(id+"F0.wireOp",EDGE,"E133"),sQuery(id+"F0.wireOp",EDGE,"E134"),sQuery(id+"F0.wireOp",EDGE,"E135"),sQuery(id+"F0.wireOp",EDGE,"E136"),sQuery(id+"F0.wireOp",EDGE,"E137"),sQuery(id+"F0.wireOp",EDGE,"E138"),sQuery(id+"F0.wireOp",EDGE,"E139"),sQuery(id+"F0.wireOp",EDGE,"E140"),sQuery(id+"F0.wireOp",EDGE,"E141"),sQuery(id+"F0.wireOp",EDGE,"E142"),sQuery(id+"F0.wireOp",EDGE,"E143"),sQuery(id+"F0.wireOp",EDGE,"E144"),sQuery(id+"F0.wireOp",EDGE,"E145"),sQuery(id+"F0.wireOp",EDGE,"E146"),sQuery(id+"F0.wireOp",EDGE,"E147"),sQuery(id+"F0.wireOp",EDGE,"E148"),sQuery(id+"F0.wireOp",EDGE,"E149"),sQuery(id+"F0.wireOp",EDGE,"E150"),sQuery(id+"F0.wireOp",EDGE,"E151"),sQuery(id+"F0.wireOp",EDGE,"E152"),sQuery(id+"F0.wireOp",EDGE,"E153"),sQuery(id+"F0.wireOp",EDGE,"E154"),sQuery(id+"F0.wireOp",EDGE,"E155"),sQuery(id+"F0.wireOp",EDGE,"E156"),sQuery(id+"F0.wireOp",EDGE,"E157"),sQuery(id+"F0.wireOp",EDGE,"E158"),sQuery(id+"F0.wireOp",EDGE,"E159"),sQuery(id+"F0.wireOp",EDGE,"E160"),sQuery(id+"F0.wireOp",EDGE,"E161"),sQuery(id+"F0.wireOp",EDGE,"E162"),sQuery(id+"F0.wireOp",EDGE,"E163"),sQuery(id+"F0.wireOp",EDGE,"E164"),sQuery(id+"F0.wireOp",EDGE,"E165"),sQuery(id+"F0.wireOp",EDGE,"E166"),sQuery(id+"F0.wireOp",EDGE,"E167"),sQuery(id+"F0.wireOp",EDGE,"E168"),sQuery(id+"F0.wireOp",EDGE,"E169"),sQuery(id+"F0.wireOp",EDGE,"E170"),sQuery(id+"F0.wireOp",EDGE,"E171"),sQuery(id+"F0.wireOp",EDGE,"E172"),sQuery(id+"F0.wireOp",EDGE,"E173"),sQuery(id+"F0.wireOp",EDGE,"E174"),sQuery(id+"F0.wireOp",EDGE,"E175"),sQuery(id+"F0.wireOp",EDGE,"E176"),sQuery(id+"F0.wireOp",EDGE,"E177"),sQuery(id+"F0.wireOp",EDGE,"E178"),sQuery(id+"F0.wireOp",EDGE,"E179"),sQuery(id+"F0.wireOp",EDGE,"E180"),sQuery(id+"F0.wireOp",EDGE,"E181"),sQuery(id+"F0.wireOp",EDGE,"E182"),sQuery(id+"F0.wireOp",EDGE,"E183"),sQuery(id+"F0.wireOp",EDGE,"E184"),sQuery(id+"F0.wireOp",EDGE,"E185"),sQuery(id+"F0.wireOp",EDGE,"E186"),sQuery(id+"F0.wireOp",EDGE,"E187"),sQuery(id+"F0.wireOp",EDGE,"E188"),sQuery(id+"F0.wireOp",EDGE,"E189"),sQuery(id+"F0.wireOp",EDGE,"E190"),sQuery(id+"F0.wireOp",EDGE,"E191"),sQuery(id+"F0.wireOp",EDGE,"E192"),sQuery(id+"F0.wireOp",EDGE,"E193"),sQuery(id+"F0.wireOp",EDGE,"E194"),sQuery(id+"F0.wireOp",EDGE,"E195"),sQuery(id+"F0.wireOp",EDGE,"E196"),sQuery(id+"F0.wireOp",EDGE,"E197"),sQuery(id+"F0.wireOp",EDGE,"E198"),sQuery(id+"F0.wireOp",EDGE,"E199"),sQuery(id+"F0.wireOp",EDGE,"E200"),sQuery(id+"F0.wireOp",EDGE,"E201"),sQuery(id+"F0.wireOp",EDGE,"E202"),sQuery(id+"F0.wireOp",EDGE,"E203"),sQuery(id+"F0.wireOp",EDGE,"E204"),sQuery(id+"F0.wireOp",EDGE,"E205"),sQuery(id+"F0.wireOp",EDGE,"E206"),sQuery(id+"F0.wireOp",EDGE,"E207"),sQuery(id+"F0.wireOp",EDGE,"E208"),sQuery(id+"F0.wireOp",EDGE,"E209"),sQuery(id+"F0.wireOp",EDGE,"E210"),sQuery(id+"F0.wireOp",EDGE,"E211"),sQuery(id+"F0.wireOp",EDGE,"E212"),sQuery(id+"F0.wireOp",EDGE,"E213"),sQuery(id+"F0.wireOp",EDGE,"E214"),sQuery(id+"F0.wireOp",EDGE,"E215"),sQuery(id+"F0.wireOp",EDGE,"E216"),sQuery(id+"F0.wireOp",EDGE,"E217"),sQuery(id+"F0.wireOp",EDGE,"E218"),sQuery(id+"F0.wireOp",EDGE,"E219"),sQuery(id+"F0.wireOp",EDGE,"E220"),sQuery(id+"F0.wireOp",EDGE,"E221"),sQuery(id+"F0.wireOp",EDGE,"E222"),sQuery(id+"F0.wireOp",EDGE,"E223"),sQuery(id+"F0.wireOp",EDGE,"E224"),sQuery(id+"F0.wireOp",EDGE,"E225"),sQuery(id+"F0.wireOp",EDGE,"E226"),sQuery(id+"F0.wireOp",EDGE,"E227"),sQuery(id+"F0.wireOp",EDGE,"E228"),sQuery(id+"F0.wireOp",EDGE,"E229"),sQuery(id+"F0.wireOp",EDGE,"E230"),sQuery(id+"F0.wireOp",EDGE,"E231"),sQuery(id+"F0.wireOp",EDGE,"E232"),sQuery(id+"F0.wireOp",EDGE,"E233"),sQuery(id+"F0.wireOp",EDGE,"E234"),sQuery(id+"F0.wireOp",EDGE,"E235"),sQuery(id+"F0.wireOp",EDGE,"E236"),sQuery(id+"F0.wireOp",EDGE,"E237"),sQuery(id+"F0.wireOp",EDGE,"E238"),sQuery(id+"F0.wireOp",EDGE,"E239"),sQuery(id+"F0.wireOp",EDGE,"E240"),sQuery(id+"F0.wireOp",EDGE,"E241"),sQuery(id+"F0.wireOp",EDGE,"E242"),sQuery(id+"F0.wireOp",EDGE,"E243"),sQuery(id+"F0.wireOp",EDGE,"E244"),sQuery(id+"F0.wireOp",EDGE,"E245"),sQuery(id+"F0.wireOp",EDGE,"E246"),sQuery(id+"F0.wireOp",EDGE,"E247"),sQuery(id+"F0.wireOp",EDGE,"E248"),sQuery(id+"F0.wireOp",EDGE,"E249"),sQuery(id+"F0.wireOp",EDGE,"E250"),sQuery(id+"F0.wireOp",EDGE,"E251"),sQuery(id+"F0.wireOp",EDGE,"E252"),sQuery(id+"F0.wireOp",EDGE,"E253"),sQuery(id+"F0.wireOp",EDGE,"E254"),sQuery(id+"F0.wireOp",EDGE,"E255"),sQuery(id+"F0.wireOp",EDGE,"E256"),sQuery(id+"F0.wireOp",EDGE,"E257"),sQuery(id+"F0.wireOp",EDGE,"E258"),sQuery(id+"F0.wireOp",EDGE,"E259"),sQuery(id+"F0.wireOp",EDGE,"E260"),sQuery(id+"F0.wireOp",EDGE,"E261"),sQuery(id+"F0.wireOp",EDGE,"E262"),sQuery(id+"F0.wireOp",EDGE,"E263"),sQuery(id+"F0.wireOp",EDGE,"E264"),sQuery(id+"F0.wireOp",EDGE,"E265"),sQuery(id+"F0.wireOp",EDGE,"E266"),sQuery(id+"F0.wireOp",EDGE,"E267"),sQuery(id+"F0.wireOp",EDGE,"E268"),sQuery(id+"F0.wireOp",EDGE,"E269"),sQuery(id+"F0.wireOp",EDGE,"E270"),sQuery(id+"F0.wireOp",EDGE,"E271"),sQuery(id+"F0.wireOp",EDGE,"E272"),sQuery(id+"F0.wireOp",EDGE,"E273"),sQuery(id+"F0.wireOp",EDGE,"E274"),sQuery(id+"F0.wireOp",EDGE,"E275"),sQuery(id+"F0.wireOp",EDGE,"E276"),sQuery(id+"F0.wireOp",EDGE,"E277"),sQuery(id+"F0.wireOp",EDGE,"E278"),sQuery(id+"F0.wireOp",EDGE,"E279"),sQuery(id+"F0.wireOp",EDGE,"E280"),sQuery(id+"F0.wireOp",EDGE,"E281"),sQuery(id+"F0.wireOp",EDGE,"E282"),sQuery(id+"F0.wireOp",EDGE,"E283"),sQuery(id+"F0.wireOp",EDGE,"E284"),sQuery(id+"F0.wireOp",EDGE,"E285"),sQuery(id+"F0.wireOp",EDGE,"E286")])],"isStart":false});
            var sketch = newSketch(context, id + "F2", { "sketchPlane" : qUnion([Q0])});
            skText(sketch, "E287", { "text": "L", "fontName": "NotoSerif-Bold.ttf"});
            skText(sketch, "E288", { "text": "M", "fontName": "NotoSerif-Bold.ttf"});
            skText(sketch, "E289", { "text": "M", "fontName": "NotoSerif-Bold.ttf"});
            skText(sketch, "E290", { "text": "G", "fontName": "NotoSerif-Bold.ttf"});
            skLineSegment(sketch, "E291.0", {"start": v(5.74, 2.35) * mm, "end": v(6.22, 3.36) * mm, "construction": true});
            skLineSegment(sketch, "E292.0", {"start": v(0.7, -8.45) * mm, "end": v(1.1, -7.6) * mm, "construction": true});
            skLineSegment(sketch, "E293.0", {"start": v(-1.5, 5.73) * mm, "end": v(-1.03, 6.75) * mm, "construction": true});
            const initialGuessF2  = {"E287": [-0.00934, -0.00423, 0.42262, 0.9063, 0.018], "E288": [-0.00394, -0.0184, 0.42262, 0.9063, 0.008], "E289": [0.0011, -0.0076, 0.42262, 0.9063, 0.008], "E290": [0.00622, 0.00336, 0.42262, 0.9063, 0.008]};
            skSetInitialGuess(sketch, initialGuessF2);
            skSolve(sketch);
        }
        {
            var Q0;
            Q0 = qSketchRegion(id + "F2", true);
            extrude(context, id + "F3", {"entities" : qUnion([Q0]), "operationType" : NewBodyOperationType.REMOVE, "oppositeDirection" : true, "depth" : (6.35 / 2) * mm, "offsetDistance" : 25 * mm});
        }
    });
